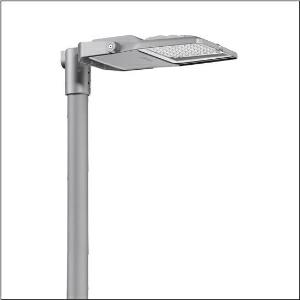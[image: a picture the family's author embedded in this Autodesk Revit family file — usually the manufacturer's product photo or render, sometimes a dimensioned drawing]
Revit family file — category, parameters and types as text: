
# Revit family: floodlight_fl_21_mini___pl33t_5xa7775c2f3a_8bfe
name_source: partatom
category: Lighting Fixtures
units: mm (PartAtom-declared; Revit-internal decimal feet)

## family parameters
Cut with Voids When Loaded = No
Host = Face
Light Source = No
Part Type = Normal
Room Calculation Point = No
Round Connector Dimension = Use Diameter
Shared = No

## types (1)
- --- (1 x LED, 12050 lm, 89 W, 3000K)
    Apparent Load = 89 VA
    CIE Flux Codes = 26 75 99 100 100
    Color Rendering = 70
    Color Temperature = 3000K
    Default Elevation = 1800 mm
    Description = Floodlight FL 21 mini, floodlight, primary light control with lens, of PMMA, primary optical cover: protective disc, of toughened safety glass, transparent, light distribution: PL33T, light emission: direct distribution, installation type: surface-mounted, LED, High Power LED, rated luminous flux: 12.050lm, luminous efficacy: 135lm/W, light colour: 730, colour temperature: 3000K, control: flexible luminous flux parameterisation, time-dependent luminous flux control, constant luminous flux control, overheat protection, pre-setting: logarithmic dimming characteristic, with terminal, 6-pole, mains connection: 220..240V, AC, 50/60Hz, start of lifetime: 89W, end of service life: 94W, reduction: 43W, luminaire housing, of diecast aluminium, powder-coated, Siteco® metallic grey (DB 702S), corrosivity category C5 mid according to DIN EN ISO 12944, sealing non-destructively replaceable, please order mast flange separately, mast bracket, of steel, galvanised, powder-coated, Siteco® metallic grey (DB 702S), Smart Interface above, protection rating (complete): IP66, insulation class (complete): insulation class II (safety insulation), certification: CE, ENEC, VDE, protection symbol: D, impact resistance: IK08, permissible operating ambient temperature: -40..+40°C, permissible operating ambient temperature for outdoor applications: -40..+50°C, standard: DIN EN 12944, LABS conformity tested according to VDMA 24364:2018-05, packaging unit: 1 piece

Light Distribution: PL33T
    Height = 70 mm
    Lamp = 1 x LED
    Lamp Light Flux = 12050 lm
    Lamp Power = 89 W
    Lamp count = 1
    Length = 485 mm
    Luminous efficacy = 135 lm/W
    Manufacturer = Siteco
    ModVariant = No
    Model = 5XA7775C2F3A
    Number of Poles = 1
    OnlyDefault = Yes
    Power Factor = 1
    Product Name = Floodlight FL 21 mini | PL33T
    Product group = floodlight | pylon annexe
    ProductGroupID = 6200
    Protection Class = Protection class II
    Protection Degree = IP 66
    RLX_Detail_Level = 1
    RLX_Emergency_Light_Flux = 0 lm
    RLX_Emergency_Type = 0
    RLX_Emergency_Type_DB = No
    RlxData = <blob elided: 100769 chars, md5=fffa17b2>
    Socket = socket
    Standby Power = 0 W
    System Light Flux = 12050 lm
    System Power = 89 W
    Type Comments = factory setting: luminous flux: 100 % | dim-lin: 254 | 456 mA
    Type Image = l_1007125.jpg
    URL = http://relux.com
    VarID = @adj_118875
    Voltage = 0 V
    Weight = 0.00 kg
    Width = 337 mm

## geometry (parser evidence)
native form markers: Blend x4, Sweep x11
no freeform markers — native parametric forms only
